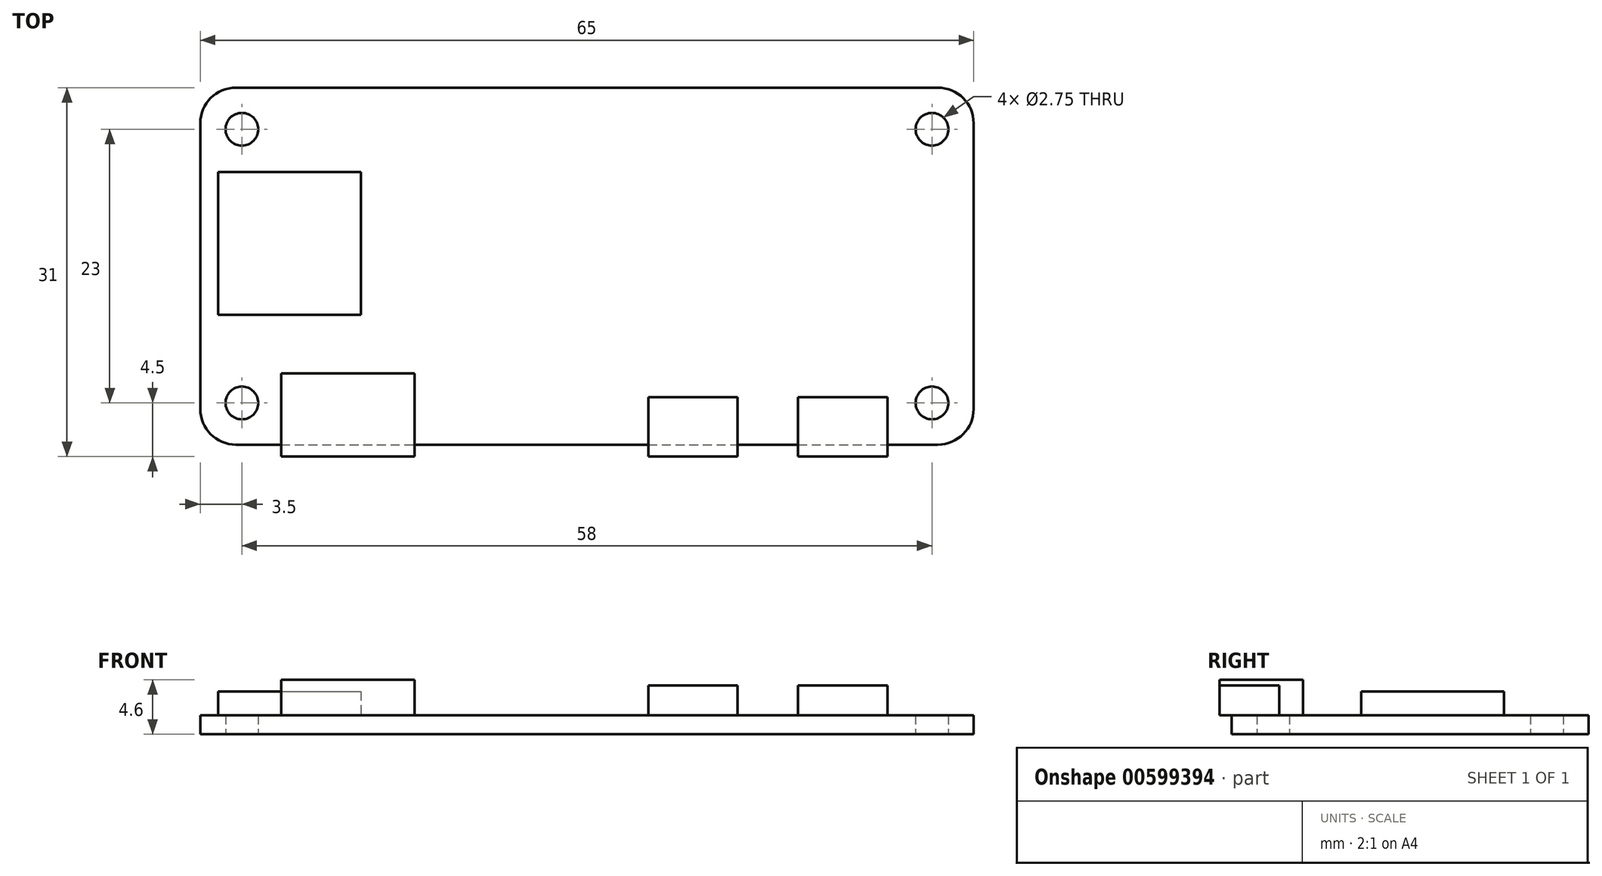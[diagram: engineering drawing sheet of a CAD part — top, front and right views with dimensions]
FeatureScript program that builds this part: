
annotation { "Feature Type Name" : "Feature", "Feature Type Description" : "" }
export const myFeature = defineFeature(function(context is Context, id is Id, definition is map)
    precondition{}
    {
        {
            var Q0;
            Q0=qCreatedBy(makeId("Top.planeOp"),FACE);
            var sketch = newSketch(context, id + "F0", { "sketchPlane" : qUnion([Q0])});
            skLineSegment(sketch, "E0.bottom", {"start": v(-32.5, 15) * mm, "end": v(32.5, 15) * mm});
            skLineSegment(sketch, "E0.top", {"start": v(-32.5, -15) * mm, "end": v(32.5, -15) * mm});
            skLineSegment(sketch, "E0.left", {"start": v(-32.5, 15) * mm, "end": v(-32.5, -15) * mm});
            skLineSegment(sketch, "E0.right", {"start": v(32.5, 15) * mm, "end": v(32.5, -15) * mm});
            skCircle(sketch, "E1", {"center": v(-29, 11.5) * mm, "radius": 1.38 * mm});
            skCircle(sketch, "E2", {"center": v(29, 11.5) * mm, "radius": 1.38 * mm});
            skCircle(sketch, "E3", {"center": v(-29, -11.5) * mm, "radius": 1.38 * mm});
            skCircle(sketch, "E4", {"center": v(29, -11.5) * mm, "radius": 1.38 * mm});
            skSolve(sketch);
        }
        {
            var Q0;
            Q0=qSketchRegion(id+"F0",true);
            extrude(context, id + "F1", {"entities" : qUnion([Q0]), "depth" : 1.6 * mm, "offsetDistance" : 25 * mm});
        }
        {
            var Q0;
            Q0=makeQuery(id+"F1.opExtrude","SWEPT_EDGE",EDGE,{"disambiguationData":[OSD([sQuery(id+"F0.wireOp",EDGE,"E0.top"),sQuery(id+"F0.wireOp",EDGE,"E0.left")])]});
            var Q1;
            Q1=makeQuery(id+"F1.opExtrude","SWEPT_EDGE",EDGE,{"disambiguationData":[OSD([sQuery(id+"F0.wireOp",EDGE,"E0.bottom"),sQuery(id+"F0.wireOp",EDGE,"E0.left")])]});
            var Q2;
            Q2=makeQuery(id+"F1.opExtrude","SWEPT_EDGE",EDGE,{"disambiguationData":[OSD([sQuery(id+"F0.wireOp",EDGE,"E0.top"),sQuery(id+"F0.wireOp",EDGE,"E0.right")])]});
            var Q3;
            Q3=makeQuery(id+"F1.opExtrude","SWEPT_EDGE",EDGE,{"disambiguationData":[OSD([sQuery(id+"F0.wireOp",EDGE,"E0.bottom"),sQuery(id+"F0.wireOp",EDGE,"E0.right")])]});
            fillet(context, id + "F2", {"entities" : qUnion([Q0, Q1, Q2, Q3]), "radius" : 3 * mm, "tangentPropagation" : true, "allowEdgeOverflow" : false});
        }
        {
            var Q0;
            Q0=makeQuery(id+"F1.opExtrude","CAP_FACE",FACE,{"disambiguationData":[OSD([sQuery(id+"F0.wireOp",EDGE,"E0.bottom"),sQuery(id+"F0.wireOp",EDGE,"E0.top"),sQuery(id+"F0.wireOp",EDGE,"E0.left"),sQuery(id+"F0.wireOp",EDGE,"E0.right"),sQuery(id+"F0.wireOp",EDGE,"E1"),sQuery(id+"F0.wireOp",EDGE,"E2"),sQuery(id+"F0.wireOp",EDGE,"E3"),sQuery(id+"F0.wireOp",EDGE,"E4")])],"isStart":false});
            var sketch = newSketch(context, id + "F3", { "sketchPlane" : qUnion([Q0])});
            skLineSegment(sketch, "E5.bottom", {"start": v(-31, 7.9) * mm, "end": v(-19, 7.9) * mm});
            skLineSegment(sketch, "E5.top", {"start": v(-31, -4.1) * mm, "end": v(-19, -4.1) * mm});
            skLineSegment(sketch, "E5.left", {"start": v(-31, 7.9) * mm, "end": v(-31, -4.1) * mm});
            skLineSegment(sketch, "E5.right", {"start": v(-19, 7.9) * mm, "end": v(-19, -4.1) * mm});
            skPoint(sketch, "E6", {"position": v(-31, 1.9) * mm});
            skSolve(sketch);
        }
        {
            var Q0;
            Q0=qSketchRegion(id+"F3",true);
            extrude(context, id + "F4", {"entities" : qUnion([Q0]), "operationType" : NewBodyOperationType.ADD, "depth" : 2 * mm, "offsetDistance" : 25 * mm});
        }
        {
            var Q0;
            Q0=makeQuery(id+"F1.opExtrude","CAP_FACE",FACE,{"disambiguationData":[OSD([sQuery(id+"F0.wireOp",EDGE,"E0.bottom"),sQuery(id+"F0.wireOp",EDGE,"E0.top"),sQuery(id+"F0.wireOp",EDGE,"E0.left"),sQuery(id+"F0.wireOp",EDGE,"E0.right"),sQuery(id+"F0.wireOp",EDGE,"E1"),sQuery(id+"F0.wireOp",EDGE,"E2"),sQuery(id+"F0.wireOp",EDGE,"E3"),sQuery(id+"F0.wireOp",EDGE,"E4")])],"isStart":false});
            var sketch = newSketch(context, id + "F5", { "sketchPlane" : qUnion([Q0])});
            skLineSegment(sketch, "E7.bottom", {"start": v(-25.7, -9) * mm, "end": v(-14.5, -9) * mm});
            skLineSegment(sketch, "E7.top", {"start": v(-25.7, -16) * mm, "end": v(-14.5, -16) * mm});
            skLineSegment(sketch, "E7.left", {"start": v(-25.7, -9) * mm, "end": v(-25.7, -16) * mm});
            skLineSegment(sketch, "E7.right", {"start": v(-14.5, -9) * mm, "end": v(-14.5, -16) * mm});
            skPoint(sketch, "E8", {"position": v(-20.1, -16) * mm});
            skSolve(sketch);
        }
        {
            var Q0;
            Q0=qSketchRegion(id+"F5",true);
            extrude(context, id + "F6", {"entities" : qUnion([Q0]), "operationType" : NewBodyOperationType.ADD, "depth" : 3 * mm, "offsetDistance" : 25 * mm});
        }
        {
            var Q0;
            Q0=makeQuery(id+"F1.opExtrude","CAP_FACE",FACE,{"disambiguationData":[OSD([sQuery(id+"F0.wireOp",EDGE,"E0.bottom"),sQuery(id+"F0.wireOp",EDGE,"E0.top"),sQuery(id+"F0.wireOp",EDGE,"E0.left"),sQuery(id+"F0.wireOp",EDGE,"E0.right"),sQuery(id+"F0.wireOp",EDGE,"E1"),sQuery(id+"F0.wireOp",EDGE,"E2"),sQuery(id+"F0.wireOp",EDGE,"E3"),sQuery(id+"F0.wireOp",EDGE,"E4")])],"isStart":false});
            var sketch = newSketch(context, id + "F7", { "sketchPlane" : qUnion([Q0])});
            skLineSegment(sketch, "E9.bottom", {"start": v(5.15, -11) * mm, "end": v(12.65, -11) * mm});
            skLineSegment(sketch, "E9.top", {"start": v(5.15, -16) * mm, "end": v(12.65, -16) * mm});
            skLineSegment(sketch, "E9.left", {"start": v(5.15, -11) * mm, "end": v(5.15, -16) * mm});
            skLineSegment(sketch, "E9.right", {"start": v(12.65, -11) * mm, "end": v(12.65, -16) * mm});
            skLineSegment(sketch, "E10.bottom", {"start": v(17.75, -11) * mm, "end": v(25.25, -11) * mm});
            skLineSegment(sketch, "E10.top", {"start": v(17.75, -16) * mm, "end": v(25.25, -16) * mm});
            skLineSegment(sketch, "E10.left", {"start": v(17.75, -11) * mm, "end": v(17.75, -16) * mm});
            skLineSegment(sketch, "E10.right", {"start": v(25.25, -11) * mm, "end": v(25.25, -16) * mm});
            skPoint(sketch, "E11", {"position": v(8.9, -16) * mm});
            skPoint(sketch, "E12", {"position": v(21.5, -16) * mm});
            skSolve(sketch);
        }
        {
            var Q0;
            Q0=qSketchRegion(id+"F7",true);
            extrude(context, id + "F8", {"entities" : qUnion([Q0]), "operationType" : NewBodyOperationType.ADD, "depth" : 2.5 * mm, "offsetDistance" : 25 * mm});
        }
    });
